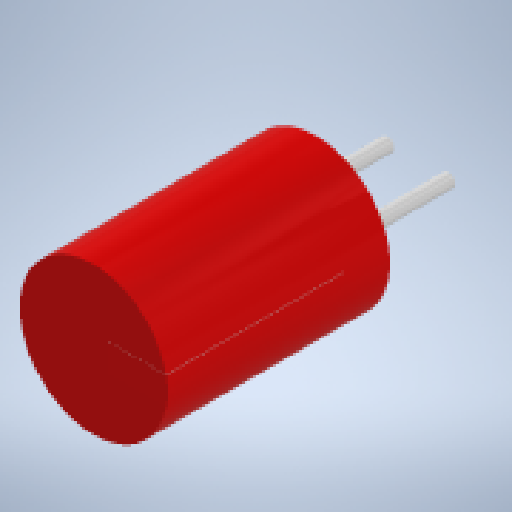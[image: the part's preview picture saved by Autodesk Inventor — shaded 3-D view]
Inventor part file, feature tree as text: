
AUTODESK INVENTOR PART (.ipt)
format: ipt  version: 2024 (Build 280153000, 153)  size: 230,400 bytes
history: native  units: mm
features: imported_body x4, fillet x2
ambient origin geometry x8: Origin, YZ Plane, XZ Plane, XY Plane, X Axis, Y Axis, Z Axis, Center Point
bodies: Solide1 (feature_tree), Solide2 (feature_tree), Solide3 (feature_tree), Solide4 (feature_tree)
feature tree (6):
  fillet  "Congé1"  Radius=3.0mm
  fillet  "Congé2"  Radius=3.0mm
  imported_body  "Base1"
  imported_body  "Base2"
  imported_body  "Base3"
  imported_body  "Base4"
